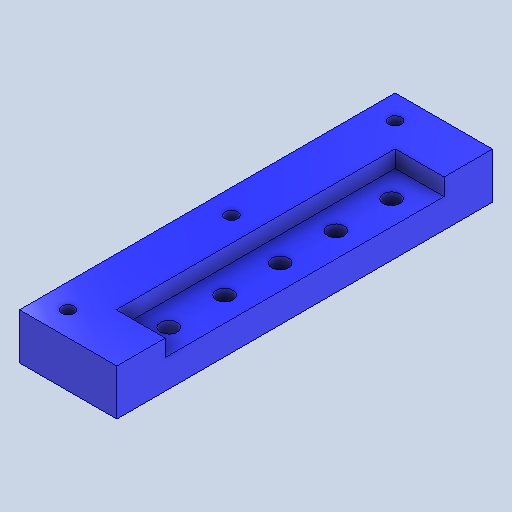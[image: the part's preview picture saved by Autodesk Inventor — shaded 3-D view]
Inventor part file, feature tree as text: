
AUTODESK INVENTOR PART (.ipt)
format: ipt  version: 2023 (Build 270158000, 158)  size: 168,448 bytes
history: native  units: in
note: dims shown in document units (in); Inventor stores cm internally (conversion verified against a paired STEP export)
features: extrude x3, sketch x1
ambient origin geometry x8: Origin, YZ Plane, XZ Plane, XY Plane, X Axis, Y Axis, Z Axis, Center Point
bodies: Solid1 (feature_tree)
feature tree (4):
  sketch  "Sketch1"  dims[d0=4.5354in d1=0.7953in d2=0.2756in d3=0.9055in d4=0.9055in d5=0.4724in d6=0.0in d7=0.0787in d8=0.0in d9=0.748in d10=0.0in d11=0.7874in d12=0.7874in d13=0.7874in d14=0.2047in]
  extrude  "Extrusion1"  Depth=0.7953in
  extrude  "Extrusion2"  Depth=0.2756in
  extrude  "Extrusion3"  Depth=0.7874in
